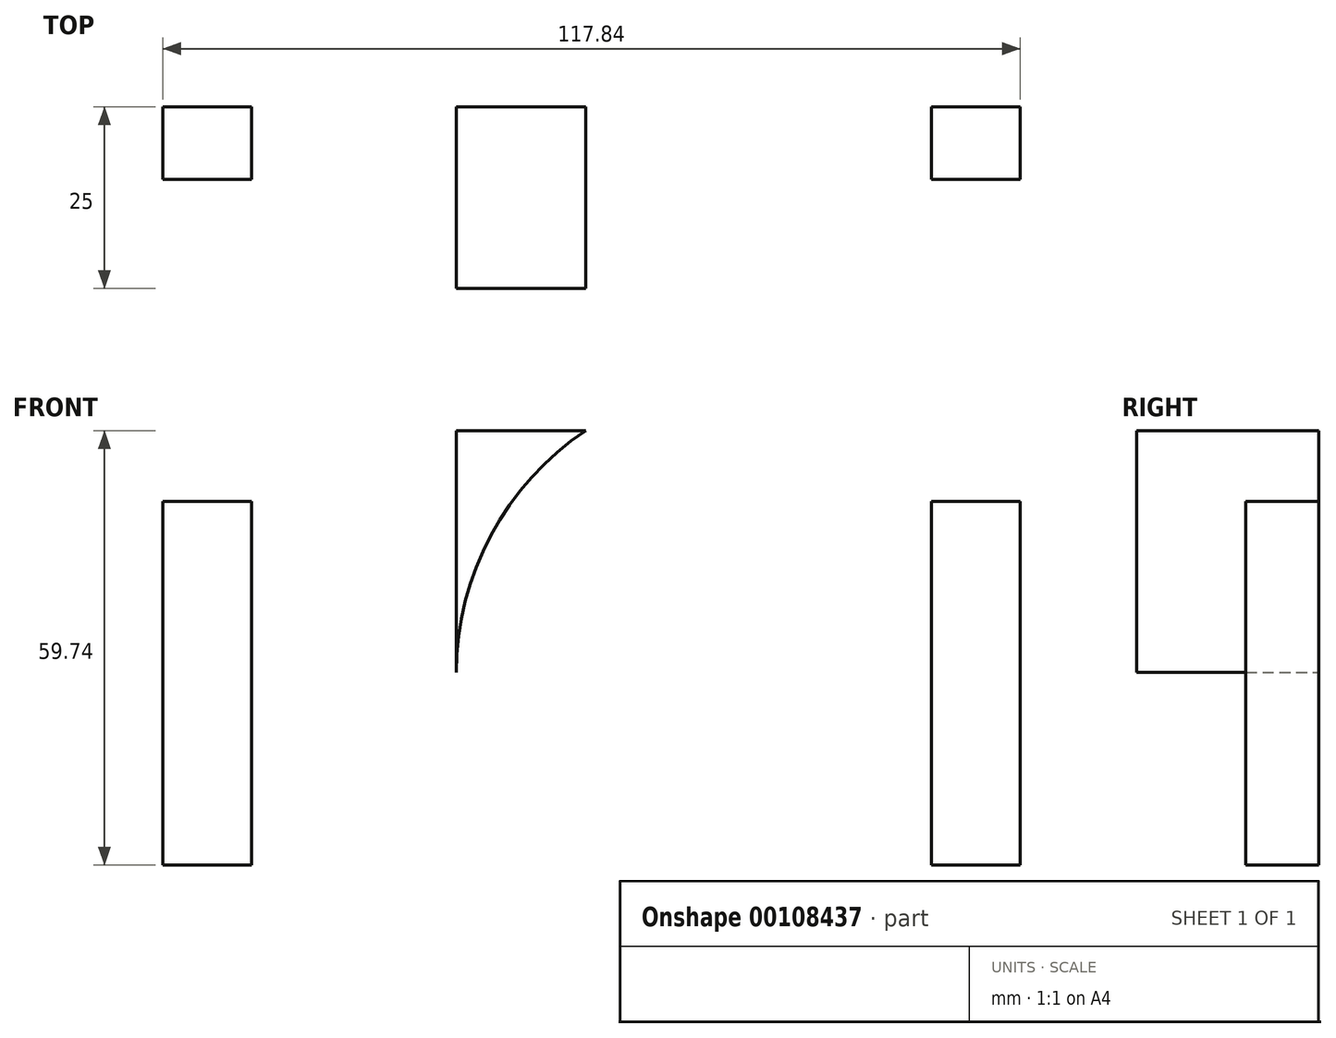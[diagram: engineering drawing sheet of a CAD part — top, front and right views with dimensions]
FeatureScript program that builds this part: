
annotation { "Feature Type Name" : "Feature", "Feature Type Description" : "" }
export const myFeature = defineFeature(function(context is Context, id is Id, definition is map)
    precondition{}
    {
        {
            var Q0;
            Q0=qCreatedBy(makeId("Front.planeOp"),FACE);
            var sketch = newSketch(context, id + "F0", { "sketchPlane" : qUnion([Q0])});
            skLineSegment(sketch, "E0.bottom", {"start": v(22.5, 25) * mm, "end": v(-22.5, 25) * mm});
            skLineSegment(sketch, "E0.top", {"start": v(22.5, -25) * mm, "end": v(-22.5, -25) * mm});
            skLineSegment(sketch, "E0.left", {"start": v(22.5, 25) * mm, "end": v(22.5, -25) * mm});
            skLineSegment(sketch, "E0.right", {"start": v(-22.5, 25) * mm, "end": v(-22.5, -25) * mm});
            skPoint(sketch, "E0.middle", {"position": v(0, 0) * mm});
            skLineSegment(sketch, "E1.bottom", {"start": v(21.45, 31.73) * mm, "end": v(18.55, 31.73) * mm});
            skLineSegment(sketch, "E1.top", {"start": v(18.55, -31.73) * mm, "end": v(-18.55, -31.73) * mm});
            skLineSegment(sketch, "E1.left", {"start": v(18.55, 31.73) * mm, "end": v(18.55, -31.73) * mm});
            skLineSegment(sketch, "E1.right", {"start": v(-18.55, 31.73) * mm, "end": v(-18.55, -31.73) * mm});
            skLineSegment(sketch, "E2.bottom", {"start": v(46.72, 15.26) * mm, "end": v(58.92, 15.26) * mm});
            skLineSegment(sketch, "E2.top", {"start": v(46.72, -34.74) * mm, "end": v(58.92, -34.74) * mm});
            skLineSegment(sketch, "E2.left", {"start": v(46.72, 15.26) * mm, "end": v(46.72, -34.74) * mm});
            skLineSegment(sketch, "E2.right", {"start": v(58.92, 15.26) * mm, "end": v(58.92, -34.74) * mm});
            skLineSegment(sketch, "E3.MirrorCS", {"start": v(-58.92, 15.26) * mm, "end": v(-58.92, -34.74) * mm});
            skLineSegment(sketch, "E4.MirrorCS", {"start": v(-46.72, 15.26) * mm, "end": v(-46.72, -34.74) * mm});
            skLineSegment(sketch, "E5.MirrorCS", {"start": v(-46.72, -34.74) * mm, "end": v(-58.92, -34.74) * mm});
            skLineSegment(sketch, "E6.MirrorCS", {"start": v(-46.72, 15.26) * mm, "end": v(-58.92, 15.26) * mm});
            skLineSegment(sketch, "E7.MirrorCS", {"start": v(-18.55, -8.27) * mm, "end": v(-18.55, -31.73) * mm});
            skPoint(sketch, "E8.visualSharp", {"position": v(-18.55, 31.73) * mm});
            skArc(sketch, "E8.filletArc", {"start": v(21.45, 31.73) * mm, "mid": v(-6.84, 20.02) * mm, "end": v(-18.55, -8.27) * mm});
            skSolve(sketch);
        }
        {
            var Q0;
            Q0=makeQuery(id+"F0.imprint","IMPRINT",FACE,{"disambiguationData":[TD([[makeQuery(id+"F0.imprint","IMPRINT",EDGE,{"derivedFrom":sQuery(id+"F0.wireOp",EDGE,"E0.bottom")}),1.0]])]});
            var Q1;
            Q1=makeQuery(id+"F0.imprint","IMPRINT",FACE,{"disambiguationData":[TD([[makeQuery(id+"F0.imprint","IMPRINT",EDGE,{"derivedFrom":sQuery(id+"F0.wireOp",EDGE,"E3.MirrorCS")}),1.0]])]});
            var Q2;
            Q2=makeQuery(id+"F0.imprint","IMPRINT",FACE,{"disambiguationData":[TD([[makeQuery(id+"F0.imprint","IMPRINT",EDGE,{"derivedFrom":sQuery(id+"F0.wireOp",EDGE,"E2.bottom")}),-1.0]])]});
            extrude(context, id + "F1", {"entities" : qUnion([Q0, Q1, Q2]), "depth" : 10 * mm});
        }
        {
            var Q0;
            Q0=makeQuery(id+"F1.opExtrude","CAP_FACE",FACE,{"disambiguationData":[OSD([sQuery(id+"F0.wireOp",EDGE,"E0.bottom"),sQuery(id+"F0.wireOp",EDGE,"E0.top"),sQuery(id+"F0.wireOp",EDGE,"E0.left"),sQuery(id+"F0.wireOp",EDGE,"E1.bottom"),sQuery(id+"F0.wireOp",EDGE,"E1.top"),sQuery(id+"F0.wireOp",EDGE,"E1.left"),sQuery(id+"F0.wireOp",EDGE,"E0.right"),sQuery(id+"F0.wireOp",EDGE,"E7.MirrorCS")])],"isStart":false});
            extrude(context, id + "F2", {"entities" : qUnion([Q0]), "operationType" : NewBodyOperationType.ADD, "depth" : 15 * mm});
        }
    });
